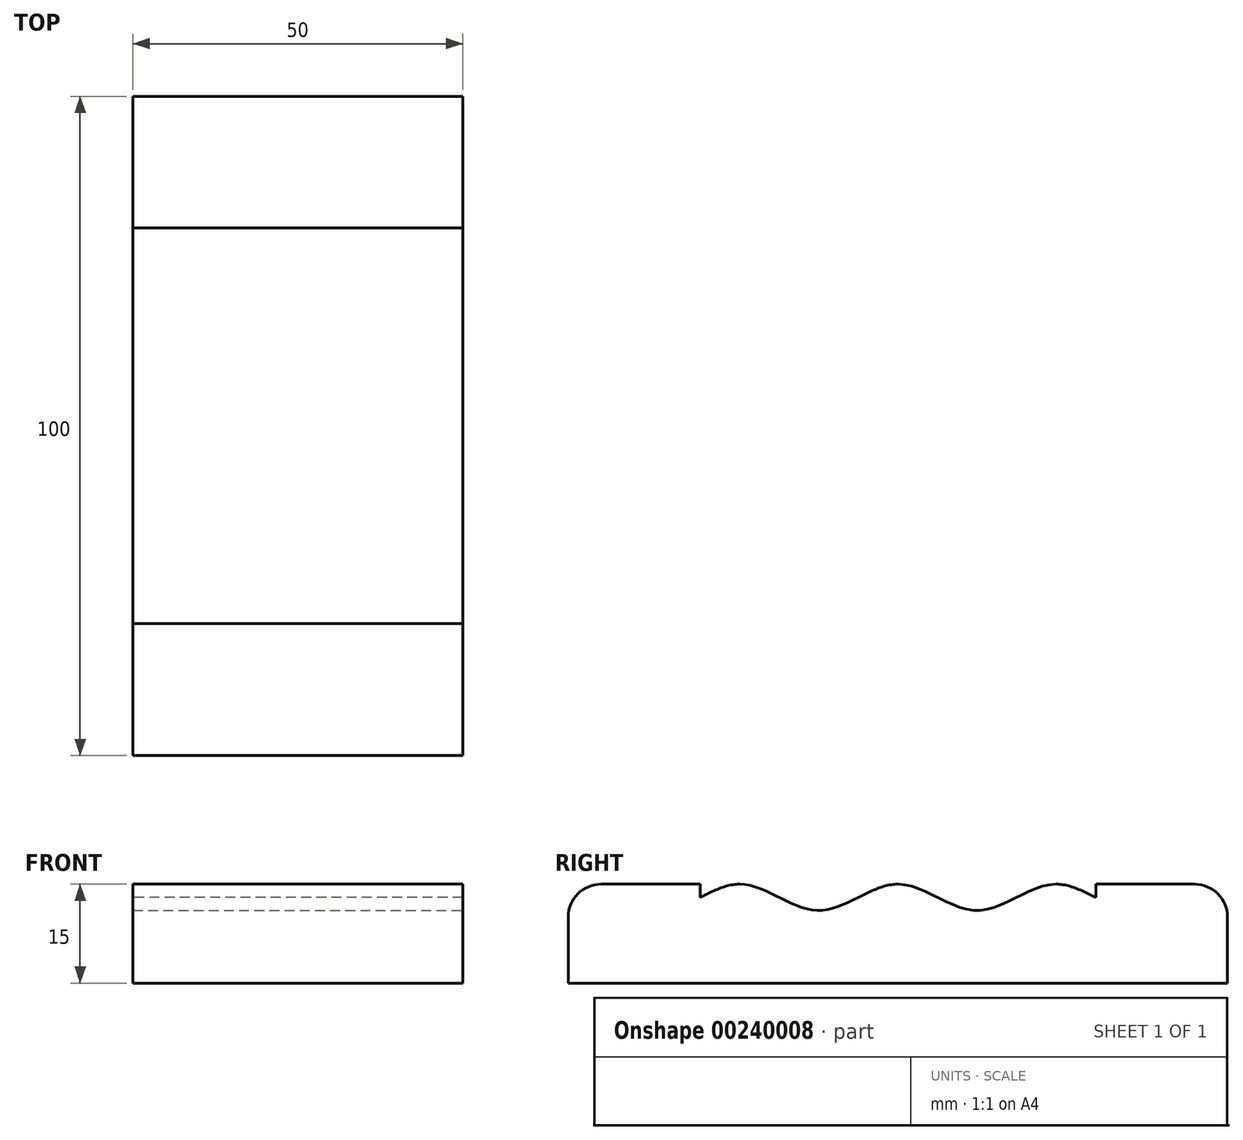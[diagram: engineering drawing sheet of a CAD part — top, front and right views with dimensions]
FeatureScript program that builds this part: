
annotation { "Feature Type Name" : "Feature", "Feature Type Description" : "" }
export const myFeature = defineFeature(function(context is Context, id is Id, definition is map)
    precondition{}
    {
        {
            var Q0;
            Q0=qCreatedBy(makeId("Right.planeOp"),FACE);
            var sketch = newSketch(context, id + "F0", { "sketchPlane" : qUnion([Q0])});
            skLineSegment(sketch, "E0.bottom", {"start": v(-45, 7.5) * mm, "end": v(45, 7.5) * mm});
            skLineSegment(sketch, "E0.top", {"start": v(-50, -7.5) * mm, "end": v(50, -7.5) * mm});
            skLineSegment(sketch, "E0.left", {"start": v(-50, 2.5) * mm, "end": v(-50, -7.5) * mm});
            skLineSegment(sketch, "E0.right", {"start": v(50, 2.5) * mm, "end": v(50, -7.5) * mm});
            skPoint(sketch, "E0.middle", {"position": v(0, 0) * mm});
            skPoint(sketch, "E1.visualSharp", {"position": v(-50, 7.5) * mm});
            skArc(sketch, "E1.filletArc", {"start": v(-45, 7.5) * mm, "mid": v(-48.54, 6.04) * mm, "end": v(-50, 2.5) * mm});
            skPoint(sketch, "E2.visualSharp", {"position": v(50, 7.5) * mm});
            skArc(sketch, "E2.filletArc", {"start": v(50, 2.5) * mm, "mid": v(48.54, 6.04) * mm, "end": v(45, 7.5) * mm});
            skLineSegment(sketch, "E3", {"start": v(-30, 12.4) * mm, "end": v(-30, -11.69) * mm, "construction": true});
            skLineSegment(sketch, "E4", {"start": v(30, 11.28) * mm, "end": v(30, -12.25) * mm, "construction": true});
            skPoint(sketch, "E5.endSnap0", {"position": v(-30, 0.36) * mm});
            skLineSegment(sketch, "E6", {"start": v(-36.3, 5.5) * mm, "end": v(41.08, 5.5) * mm, "construction": true});
            skLineSegment(sketch, "E7", {"start": v(-36.65, 3.5) * mm, "end": v(41.96, 3.5) * mm, "construction": true});
            skLineSegment(sketch, "E8", {"start": v(-24, 9.95) * mm, "end": v(-24, 0.7) * mm, "construction": true});
            skLineSegment(sketch, "E9", {"start": v(-18, 10.22) * mm, "end": v(-18, 0) * mm, "construction": true});
            skLineSegment(sketch, "E10", {"start": v(-12, 8.82) * mm, "end": v(-12, 0) * mm, "construction": true});
            skLineSegment(sketch, "E11.1.0.0", {"start": v(-6, 8.82) * mm, "end": v(-6, 0) * mm, "construction": true});
            skLineSegment(sketch, "E11.2.0.0", {"start": v(0, 8.82) * mm, "end": v(0, 0) * mm, "construction": true});
            skLineSegment(sketch, "E11.3.0.0", {"start": v(6, 8.82) * mm, "end": v(6, 0) * mm, "construction": true});
            skLineSegment(sketch, "E11.4.0.0", {"start": v(12, 8.82) * mm, "end": v(12, 0) * mm, "construction": true});
            skLineSegment(sketch, "E11.5.0.0", {"start": v(18, 8.82) * mm, "end": v(18, 0) * mm, "construction": true});
            skLineSegment(sketch, "E11.6.0.0", {"start": v(24, 8.82) * mm, "end": v(24, 0) * mm, "construction": true});
            skLineSegment(sketch, "E11.direction1", {"start": v(-12, 0) * mm, "end": v(-6, 0) * mm, "construction": true});
            skPoint(sketch, "E12.3.internal.snap0", {"position": v(-12, 4.41) * mm});
            skFitSpline(sketch, "E12", {"points": [v(-30, 5.5) * mm, v(-24, 7.5) * mm, v(-18, 5.5) * mm, v(-12, 3.5) * mm, v(-6, 5.5) * mm], "startDerivative": vector(24, 12) * mm, "endDerivative": vector(24, 12) * mm});
            skFitSpline(sketch, "E13", {"points": [v(-6, 5.5) * mm, v(0, 7.5) * mm, v(6, 5.5) * mm, v(12, 3.5) * mm, v(18, 5.5) * mm, v(24, 7.5) * mm, v(30, 5.5) * mm], "startDerivative": vector(36, 18) * mm, "endDerivative": vector(36, -18) * mm});
            skLineSegment(sketch, "E14", {"start": v(-30, 5.5) * mm, "end": v(-30, 0.36) * mm});
            skLineSegment(sketch, "E15", {"start": v(30, 0) * mm, "end": v(30, 5.5) * mm});
            skLineSegment(sketch, "E16", {"start": v(-30, 5.5) * mm, "end": v(-30, 11.28) * mm});
            skLineSegment(sketch, "E17", {"start": v(-30, 11.28) * mm, "end": v(30, 11.28) * mm});
            skLineSegment(sketch, "E18", {"start": v(30, 5.5) * mm, "end": v(30, 11.28) * mm});
            skSolve(sketch);
        }
        {
            var Q0;
            Q0=makeQuery(id+"F0.imprint","IMPRINT",FACE,{"disambiguationData":[TD([[makeQuery(id+"F0.imprint","IMPRINT",EDGE,{"derivedFrom":sQuery(id+"F0.wireOp",EDGE,"E0.top")}),1.0]])]});
            extrude(context, id + "F1", {"entities" : qUnion([Q0]), "endBound" : BoundingType.SYMMETRIC, "depth" : 50 * mm});
        }
    });
